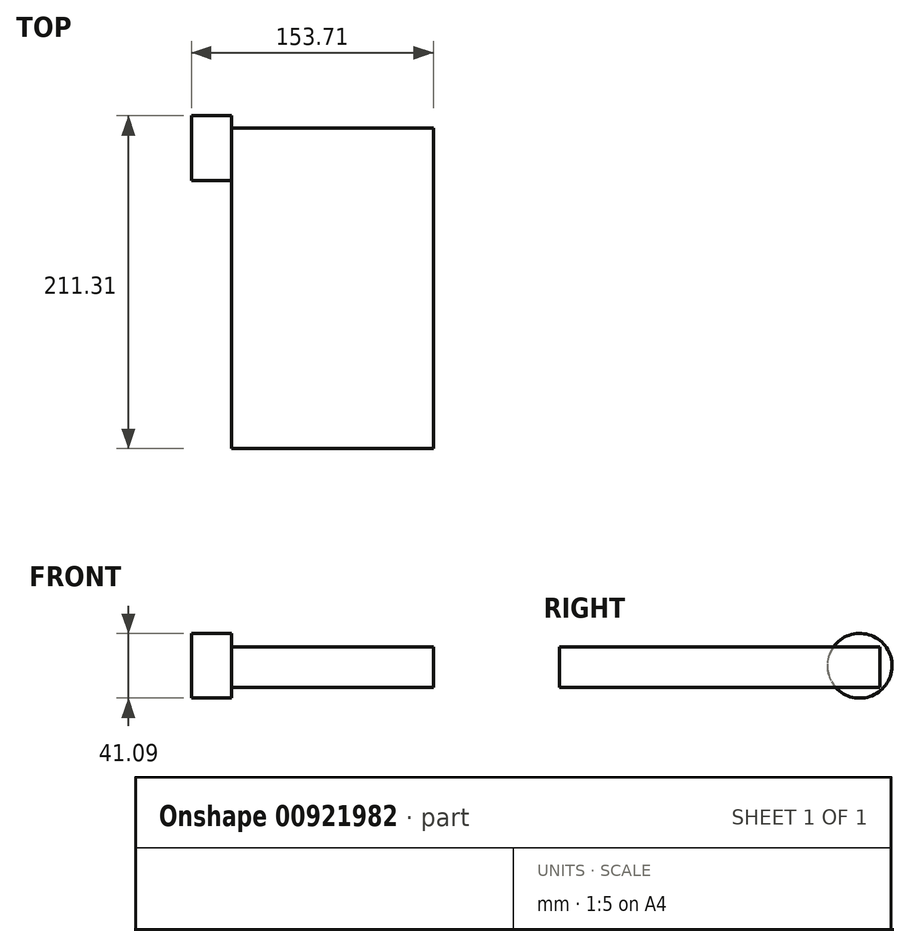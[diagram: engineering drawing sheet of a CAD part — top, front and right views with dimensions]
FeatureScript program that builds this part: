
annotation { "Feature Type Name" : "Feature", "Feature Type Description" : "" }
export const myFeature = defineFeature(function(context is Context, id is Id, definition is map)
    precondition{}
    {
        {
            var Q0;
            Q0=qCreatedBy(makeId("Front.planeOp"),FACE);
            var sketch = newSketch(context, id + "F0", { "sketchPlane" : qUnion([Q0])});
            skLineSegment(sketch, "E0.bottom", {"start": v(-65.71, 25.66) * mm, "end": v(62.6, 25.66) * mm});
            skLineSegment(sketch, "E0.top", {"start": v(-65.71, 0) * mm, "end": v(62.6, 0) * mm});
            skLineSegment(sketch, "E0.left", {"start": v(-65.71, 25.66) * mm, "end": v(-65.71, 0) * mm});
            skLineSegment(sketch, "E0.right", {"start": v(62.6, 25.66) * mm, "end": v(62.6, 0) * mm});
            skSolve(sketch);
        }
        {
            var Q0;
            Q0=makeQuery(id+"F0.imprint","IMPRINT",FACE,{"disambiguationData":[TD([[makeQuery(id+"F0.imprint","IMPRINT",EDGE,{"derivedFrom":sQuery(id+"F0.wireOp",EDGE,"E0.bottom")}),-1.0]])]});
            extrude(context, id + "F1", {"entities" : qUnion([Q0]), "oppositeDirection" : true, "depth" : 203.45 * mm, "offsetDistance" : 25.4 * mm});
        }
        {
            var Q0;
            Q0=makeQuery(id+"F1.opExtrude","SWEPT_FACE",FACE,{"disambiguationData":[OSD([sQuery(id+"F0.wireOp",EDGE,"E0.left")])]});
            var sketch = newSketch(context, id + "F2", { "sketchPlane" : qUnion([Q0])});
            skCircle(sketch, "E1", {"center": v(-190.77, 13.7) * mm, "radius": 20.54 * mm});
            skSolve(sketch);
        }
        {
            var Q0;
            Q0 = qSketchRegion(id + "F2", true);
            extrude(context, id + "F3", {"entities" : qUnion([Q0]), "operationType" : NewBodyOperationType.ADD, "depth" : 25.4 * mm, "offsetDistance" : 25.4 * mm});
        }
    });
